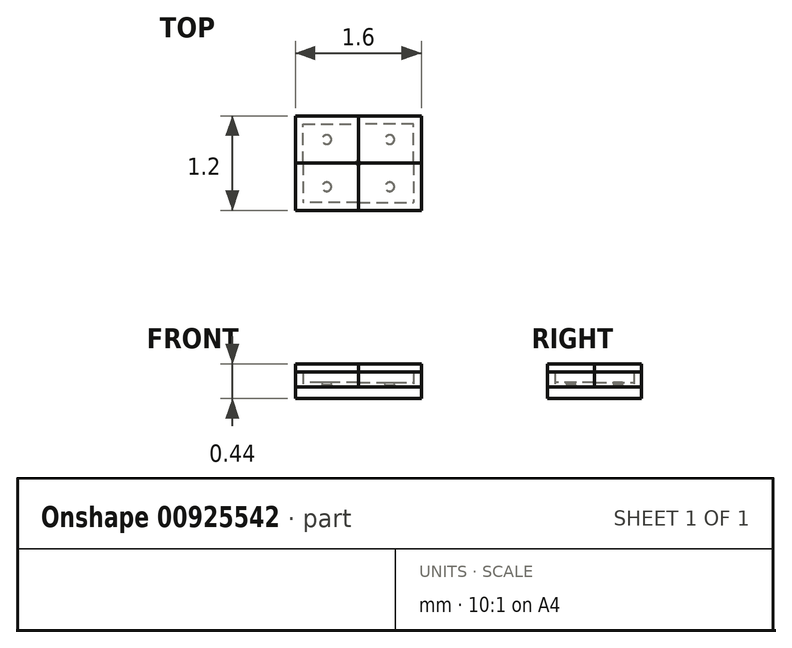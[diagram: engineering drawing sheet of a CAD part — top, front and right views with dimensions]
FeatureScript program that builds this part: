
annotation { "Feature Type Name" : "Feature", "Feature Type Description" : "" }
export const myFeature = defineFeature(function(context is Context, id is Id, definition is map)
    precondition{}
    {
        {
            var Q0;
            Q0=qCreatedBy(makeId("Top.planeOp"),FACE);
            var sketch = newSketch(context, id + "F0", { "sketchPlane" : qUnion([Q0])});
            skLineSegment(sketch, "E0.bottom", {"start": v(0, 0) * mm, "end": v(-0.8, 0) * mm});
            skLineSegment(sketch, "E0.top", {"start": v(0, 0.6) * mm, "end": v(-0.8, 0.6) * mm});
            skLineSegment(sketch, "E0.left", {"start": v(0, 0) * mm, "end": v(0, 0.6) * mm});
            skLineSegment(sketch, "E0.right", {"start": v(-0.8, 0) * mm, "end": v(-0.8, 0.6) * mm});
            skLineSegment(sketch, "E1", {"start": v(-0.8, 0.3) * mm, "end": v(0, 0.3) * mm, "construction": true});
            skSolve(sketch);
        }
        {
            var Q0;
            Q0 = qSketchRegion(id + "F0", true);
            extrude(context, id + "F1", {"entities" : qUnion([Q0]), "depth" : 0.15 * mm, "offsetDistance" : 25.4 * mm});
        }
        {
            var Q0;
            Q0=makeQuery(id+"F1.opExtrude","SWEPT_FACE",FACE,{"disambiguationData":[OSD([sQuery(id+"F0.wireOp",EDGE,"E0.left")])]});
            cPlane(context, id + "F2", {"entities" : qUnion([Q0]), "cplaneType" : CPlaneType.OFFSET, "offset" : 0.4 * mm, "oppositeDirection" : true, "width" : 152.4 * mm, "height" : 152.4 * mm});
        }
        {
            var Q0;
            {var subQ0=makeQuery(id+"F1.opExtrude","CAP_FACE",FACE,{"disambiguationData":[OSD([sQuery(id+"F0.wireOp",EDGE,"E0.bottom"),sQuery(id+"F0.wireOp",EDGE,"E0.top"),sQuery(id+"F0.wireOp",EDGE,"E0.left"),sQuery(id+"F0.wireOp",EDGE,"E0.right")])],"isStart":false});var subQ1=makeQuery(id+"F15.opPattern","COPY",FACE,{"derivedFrom":subQ0,"instanceName":"1"});Q0=makeQuery(id+"F17.opBoolean","MERGE",FACE,{"derivedFrom":[subQ0,subQ1,makeQuery(id+"F16.opPattern","COPY",FACE,{"derivedFrom":subQ0,"instanceName":"1"}),makeQuery(id+"F16.opPattern","COPY",FACE,{"derivedFrom":subQ1,"instanceName":"1"})]});}
            var sketch = newSketch(context, id + "F3", { "sketchPlane" : qUnion([Q0])});
            skCircle(sketch, "E2", {"center": v(-0.4, 0.3) * mm, "radius": 0.06 * mm});
            skLineSegment(sketch, "E3", {"start": v(-0.8, 0.3) * mm, "end": v(0, 0.3) * mm, "construction": true});
            skSolve(sketch);
        }
        {
            var Q0;
            Q0 = qSketchRegion(id + "F3", true);
            extrude(context, id + "F4", {"entities" : qUnion([Q0]), "depth" : 0.03 * mm, "offsetDistance" : 25.4 * mm});
        }
        {
            var Q0;
            Q0=qCreatedBy(id+"F2.planeOp",FACE);
            var sketch = newSketch(context, id + "F5", { "sketchPlane" : qUnion([Q0])});
            skLineSegment(sketch, "E4", {"start": v(0.24, 0.18) * mm, "end": v(0.3, 0.18) * mm});
            skArc(sketch, "E5", {"start": v(0.24, 0.18) * mm, "mid": v(0.24, 0.2) * mm, "end": v(0.24, 0.2) * mm});
            skLineSegment(sketch, "E6", {"start": v(0.3, 0.2) * mm, "end": v(0.3, 0.18) * mm});
            skLineSegment(sketch, "E7", {"start": v(0.24, 0.2) * mm, "end": v(0.3, 0.2) * mm});
            skLineSegment(sketch, "E8", {"start": v(0.3, 0.2) * mm, "end": v(0.3, 0.2) * mm});
            skPoint(sketch, "E9.orphan", {"position": v(0.36, 0.18) * mm});
            skSolve(sketch);
        }
        {
            var Q0;
            Q0=makeQuery(id+"F5.imprint","IMPRINT",FACE,{"disambiguationData":[TD([[makeQuery(id+"F5.imprint","IMPRINT",EDGE,{"derivedFrom":sQuery(id+"F5.wireOp",EDGE,"E4")}),1.0]])]});
            var Q1;
            Q1=sQuery(id+"F5.wireOp",EDGE,"E8");
            revolve(context, id + "F6", {"surfaceOperationType" : NewSurfaceOperationType.NEW, "entities" : qUnion([Q0]), "axis" : qUnion([Q1]), "revolveType" : RevolveType.FULL});
        }
        {
            var Q0;
            Q0=makeQuery(id+"F6.opRevolve","SWEPT_FACE",FACE,{"disambiguationData":[OSD([sQuery(id+"F5.wireOp",EDGE,"E7")])]});
            var sketch = newSketch(context, id + "F7", { "sketchPlane" : qUnion([Q0])});
            skLineSegment(sketch, "E10.bottom", {"start": v(0, 0) * mm, "end": v(-0.7, 0) * mm});
            skLineSegment(sketch, "E10.top", {"start": v(0, 0.5) * mm, "end": v(-0.7, 0.5) * mm});
            skLineSegment(sketch, "E10.left", {"start": v(0, 0) * mm, "end": v(0, 0.5) * mm});
            skLineSegment(sketch, "E10.right", {"start": v(-0.7, 0) * mm, "end": v(-0.7, 0.5) * mm});
            skLineSegment(sketch, "E11.top", {"start": v(0, 0) * mm, "end": v(-0.03, 0) * mm});
            skLineSegment(sketch, "E11.left", {"start": v(0, 0.03) * mm, "end": v(0, 0) * mm});
            skSolve(sketch);
        }
        {
            var Q0;
            Q0 = qSketchRegion(id + "F7", true);
            extrude(context, id + "F8", {"entities" : qUnion([Q0]), "depth" : 0.13 * mm, "offsetDistance" : 25.4 * mm});
        }
        {
            var Q0;
            Q0=makeQuery(id+"F8.opExtrude","CAP_FACE",FACE,{"disambiguationData":[OSD([sQuery(id+"F7.wireOp",EDGE,"E10.bottom"),sQuery(id+"F7.wireOp",EDGE,"E10.top"),sQuery(id+"F7.wireOp",EDGE,"E10.left"),sQuery(id+"F7.wireOp",EDGE,"E10.right")])],"isStart":false});
            var sketch = newSketch(context, id + "F9", { "sketchPlane" : qUnion([Q0])});
            skLineSegment(sketch, "E12.bottom", {"start": v(-0.7, 0) * mm, "end": v(-0.8, 0) * mm});
            skLineSegment(sketch, "E12.top", {"start": v(-0.7, 0.6) * mm, "end": v(-0.8, 0.6) * mm});
            skLineSegment(sketch, "E12.left", {"start": v(-0.7, 0) * mm, "end": v(-0.7, 0.6) * mm});
            skLineSegment(sketch, "E12.right", {"start": v(-0.8, 0) * mm, "end": v(-0.8, 0.6) * mm});
            skLineSegment(sketch, "E13.bottom", {"start": v(-0.7, 0.6) * mm, "end": v(0, 0.6) * mm});
            skLineSegment(sketch, "E13.top", {"start": v(-0.7, 0.5) * mm, "end": v(0, 0.5) * mm});
            skLineSegment(sketch, "E13.left", {"start": v(-0.7, 0.6) * mm, "end": v(-0.7, 0.5) * mm});
            skLineSegment(sketch, "E13.right", {"start": v(0, 0.6) * mm, "end": v(0, 0.5) * mm});
            skLineSegment(sketch, "E14.top", {"start": v(-0.7, 0) * mm, "end": v(0, 0) * mm});
            skLineSegment(sketch, "E14.left", {"start": v(-0.7, 0.5) * mm, "end": v(-0.7, 0) * mm});
            skLineSegment(sketch, "E14.right", {"start": v(0, 0.5) * mm, "end": v(0, 0) * mm});
            skSolve(sketch);
        }
        {
            var Q0;
            Q0 = qSketchRegion(id + "F9", true);
            extrude(context, id + "F10", {"entities" : qUnion([Q0]), "depth" : 0.1 * mm, "offsetDistance" : 25.4 * mm});
        }
        {
            var Q0;
            Q0=makeQuery(id+"F7.imprint","IMPRINT",FACE,{"disambiguationData":[TD([[makeQuery(id+"F7.imprint","IMPRINT",EDGE,{"derivedFrom":sQuery(id+"F7.wireOp",EDGE,"E10.bottom")}),-1.0]])]});
            var sketch = newSketch(context, id + "F11", { "sketchPlane" : qUnion([Q0])});
            skLineSegment(sketch, "E15.bottom", {"start": v(0, 0) * mm, "end": v(-0.03, 0) * mm});
            skLineSegment(sketch, "E15.top", {"start": v(0, 0.03) * mm, "end": v(-0.03, 0.03) * mm});
            skLineSegment(sketch, "E15.left", {"start": v(0, 0) * mm, "end": v(0, 0.03) * mm});
            skLineSegment(sketch, "E15.right", {"start": v(-0.03, 0) * mm, "end": v(-0.03, 0.03) * mm});
            skSolve(sketch);
        }
        {
            var Q0;
            Q0=makeQuery(id+"F1.opExtrude","CAP_FACE",FACE,{"disambiguationData":[OSD([sQuery(id+"F0.wireOp",EDGE,"E0.bottom"),sQuery(id+"F0.wireOp",EDGE,"E0.top"),sQuery(id+"F0.wireOp",EDGE,"E0.left"),sQuery(id+"F0.wireOp",EDGE,"E0.right")])],"isStart":false});
            var sketch = newSketch(context, id + "F12", { "sketchPlane" : qUnion([Q0])});
            skLineSegment(sketch, "E16", {"start": v(0, 0.6) * mm, "end": v(-0.8, 0.6) * mm});
            skLineSegment(sketch, "E17", {"start": v(-0.8, 0.6) * mm, "end": v(-0.8, 0) * mm});
            skLineSegment(sketch, "E18", {"start": v(-0.8, 0) * mm, "end": v(-0.7, 0) * mm});
            skLineSegment(sketch, "E19", {"start": v(-0.7, 0) * mm, "end": v(-0.7, 0.5) * mm});
            skLineSegment(sketch, "E20", {"start": v(-0.7, 0.5) * mm, "end": v(0, 0.5) * mm});
            skLineSegment(sketch, "E21", {"start": v(0, 0.5) * mm, "end": v(0, 0.6) * mm});
            skSolve(sketch);
        }
        {
            var Q0;
            Q0 = qSketchRegion(id + "F11", true);
            extrude(context, id + "F13", {"entities" : qUnion([Q0]), "depth" : 0 * mm, "offsetDistance" : 25.4 * mm});
        }
        {
            var Q0;
            Q0 = qSketchRegion(id + "F12", true);
            extrude(context, id + "F14", {"entities" : qUnion([Q0]), "depth" : 0.19 * mm, "offsetDistance" : 25.4 * mm});
        }
        {
            var Q0;
            Q0=makeQuery(id+"F8.opExtrude","SWEPT_BODY",BODY,{"disambiguationData":[OSD([sQuery(id+"F7.wireOp",EDGE,"E10.bottom"),sQuery(id+"F7.wireOp",EDGE,"E10.top"),sQuery(id+"F7.wireOp",EDGE,"E10.left"),sQuery(id+"F7.wireOp",EDGE,"E10.right"),sQuery(id+"F7.wireOp",EDGE,"E11.top"),sQuery(id+"F7.wireOp",EDGE,"E11.left")])]});
            var Q1;
            Q1=makeQuery(id+"F10.opExtrude","SWEPT_BODY",BODY,{"disambiguationData":[OSD([sQuery(id+"F9.wireOp",EDGE,"E12.bottom"),sQuery(id+"F9.wireOp",EDGE,"E12.top"),sQuery(id+"F9.wireOp",EDGE,"E12.right"),sQuery(id+"F9.wireOp",EDGE,"E13.bottom"),sQuery(id+"F9.wireOp",EDGE,"E13.right"),sQuery(id+"F9.wireOp",EDGE,"E14.top"),sQuery(id+"F9.wireOp",EDGE,"E14.right")])]});
            var Q2;
            Q2=makeQuery(id+"F6.opRevolve","SWEPT_BODY",BODY,{"disambiguationData":[OSD([sQuery(id+"F5.wireOp",EDGE,"E4"),sQuery(id+"F5.wireOp",EDGE,"E5"),sQuery(id+"F5.wireOp",EDGE,"E6"),sQuery(id+"F5.wireOp",EDGE,"E7"),sQuery(id+"F5.wireOp",EDGE,"E8")])]});
            var Q3;
            Q3=makeQuery(id+"F13.opExtrude","SWEPT_BODY",BODY,{"disambiguationData":[OSD([sQuery(id+"F11.wireOp",EDGE,"E15.bottom"),sQuery(id+"F11.wireOp",EDGE,"E15.top"),sQuery(id+"F11.wireOp",EDGE,"E15.left"),sQuery(id+"F11.wireOp",EDGE,"E15.right")])]});
            var Q4;
            Q4=makeQuery(id+"F1.opExtrude","SWEPT_BODY",BODY,{"disambiguationData":[OSD([sQuery(id+"F0.wireOp",EDGE,"E0.bottom"),sQuery(id+"F0.wireOp",EDGE,"E0.top"),sQuery(id+"F0.wireOp",EDGE,"E0.left"),sQuery(id+"F0.wireOp",EDGE,"E0.right")])]});
            var Q5;
            Q5=makeQuery(id+"F4.opExtrude","SWEPT_BODY",BODY,{"disambiguationData":[OSD([sQuery(id+"F3.wireOp",EDGE,"E2")])]});
            var Q6;
            Q6=makeQuery(id+"F14.opExtrude","SWEPT_BODY",BODY,{"disambiguationData":[OSD([sQuery(id+"F12.wireOp",EDGE,"E16"),sQuery(id+"F12.wireOp",EDGE,"E17"),sQuery(id+"F12.wireOp",EDGE,"E18"),sQuery(id+"F12.wireOp",EDGE,"E19"),sQuery(id+"F12.wireOp",EDGE,"E20"),sQuery(id+"F12.wireOp",EDGE,"E21")])]});
            var Q7;
            Q7=makeQuery(id+"F8.opExtrude","SWEPT_FACE",FACE,{"disambiguationData":[OSD([sQuery(id+"F7.wireOp",EDGE,"E10.left")])]});
            mirror(context, id + "F15", {"entities" : qUnion([Q0, Q1, Q2, Q3, Q4, Q5, Q6]), "mirrorPlane" : qUnion([Q7])});
        }
        {
            var Q0;
            Q0=makeQuery(id+"F15.opPattern","COPY",BODY,{"derivedFrom":makeQuery(id+"F10.opExtrude","SWEPT_BODY",BODY,{"disambiguationData":[OSD([sQuery(id+"F9.wireOp",EDGE,"E12.bottom"),sQuery(id+"F9.wireOp",EDGE,"E12.top"),sQuery(id+"F9.wireOp",EDGE,"E12.right"),sQuery(id+"F9.wireOp",EDGE,"E13.bottom"),sQuery(id+"F9.wireOp",EDGE,"E13.right"),sQuery(id+"F9.wireOp",EDGE,"E14.top"),sQuery(id+"F9.wireOp",EDGE,"E14.right")])]}),"instanceName":"1"});
            var Q1;
            Q1=makeQuery(id+"F15.opPattern","COPY",BODY,{"derivedFrom":makeQuery(id+"F13.opExtrude","SWEPT_BODY",BODY,{"disambiguationData":[OSD([sQuery(id+"F11.wireOp",EDGE,"E15.bottom"),sQuery(id+"F11.wireOp",EDGE,"E15.top"),sQuery(id+"F11.wireOp",EDGE,"E15.left"),sQuery(id+"F11.wireOp",EDGE,"E15.right")])]}),"instanceName":"1"});
            var Q2;
            Q2=makeQuery(id+"F15.opPattern","COPY",BODY,{"derivedFrom":makeQuery(id+"F8.opExtrude","SWEPT_BODY",BODY,{"disambiguationData":[OSD([sQuery(id+"F7.wireOp",EDGE,"E10.bottom"),sQuery(id+"F7.wireOp",EDGE,"E10.top"),sQuery(id+"F7.wireOp",EDGE,"E10.left"),sQuery(id+"F7.wireOp",EDGE,"E10.right"),sQuery(id+"F7.wireOp",EDGE,"E11.top"),sQuery(id+"F7.wireOp",EDGE,"E11.left")])]}),"instanceName":"1"});
            var Q3;
            Q3=makeQuery(id+"F10.opExtrude","SWEPT_BODY",BODY,{"disambiguationData":[OSD([sQuery(id+"F9.wireOp",EDGE,"E12.bottom"),sQuery(id+"F9.wireOp",EDGE,"E12.top"),sQuery(id+"F9.wireOp",EDGE,"E12.right"),sQuery(id+"F9.wireOp",EDGE,"E13.bottom"),sQuery(id+"F9.wireOp",EDGE,"E13.right"),sQuery(id+"F9.wireOp",EDGE,"E14.top"),sQuery(id+"F9.wireOp",EDGE,"E14.right")])]});
            var Q4;
            Q4=makeQuery(id+"F13.opExtrude","SWEPT_BODY",BODY,{"disambiguationData":[OSD([sQuery(id+"F11.wireOp",EDGE,"E15.bottom"),sQuery(id+"F11.wireOp",EDGE,"E15.top"),sQuery(id+"F11.wireOp",EDGE,"E15.left"),sQuery(id+"F11.wireOp",EDGE,"E15.right")])]});
            var Q5;
            Q5=makeQuery(id+"F15.opPattern","COPY",BODY,{"derivedFrom":makeQuery(id+"F1.opExtrude","SWEPT_BODY",BODY,{"disambiguationData":[OSD([sQuery(id+"F0.wireOp",EDGE,"E0.bottom"),sQuery(id+"F0.wireOp",EDGE,"E0.top"),sQuery(id+"F0.wireOp",EDGE,"E0.left"),sQuery(id+"F0.wireOp",EDGE,"E0.right")])]}),"instanceName":"1"});
            var Q6;
            Q6=makeQuery(id+"F8.opExtrude","SWEPT_BODY",BODY,{"disambiguationData":[OSD([sQuery(id+"F7.wireOp",EDGE,"E10.bottom"),sQuery(id+"F7.wireOp",EDGE,"E10.top"),sQuery(id+"F7.wireOp",EDGE,"E10.left"),sQuery(id+"F7.wireOp",EDGE,"E10.right"),sQuery(id+"F7.wireOp",EDGE,"E11.top"),sQuery(id+"F7.wireOp",EDGE,"E11.left")])]});
            var Q7;
            Q7=makeQuery(id+"F6.opRevolve","SWEPT_BODY",BODY,{"disambiguationData":[OSD([sQuery(id+"F5.wireOp",EDGE,"E4"),sQuery(id+"F5.wireOp",EDGE,"E5"),sQuery(id+"F5.wireOp",EDGE,"E6"),sQuery(id+"F5.wireOp",EDGE,"E7"),sQuery(id+"F5.wireOp",EDGE,"E8")])]});
            var Q8;
            Q8=makeQuery(id+"F1.opExtrude","SWEPT_BODY",BODY,{"disambiguationData":[OSD([sQuery(id+"F0.wireOp",EDGE,"E0.bottom"),sQuery(id+"F0.wireOp",EDGE,"E0.top"),sQuery(id+"F0.wireOp",EDGE,"E0.left"),sQuery(id+"F0.wireOp",EDGE,"E0.right")])]});
            var Q9;
            Q9=makeQuery(id+"F15.opPattern","COPY",BODY,{"derivedFrom":makeQuery(id+"F6.opRevolve","SWEPT_BODY",BODY,{"disambiguationData":[OSD([sQuery(id+"F5.wireOp",EDGE,"E4"),sQuery(id+"F5.wireOp",EDGE,"E5"),sQuery(id+"F5.wireOp",EDGE,"E6"),sQuery(id+"F5.wireOp",EDGE,"E7"),sQuery(id+"F5.wireOp",EDGE,"E8")])]}),"instanceName":"1"});
            var Q10;
            Q10=makeQuery(id+"F4.opExtrude","SWEPT_BODY",BODY,{"disambiguationData":[OSD([sQuery(id+"F3.wireOp",EDGE,"E2")])]});
            var Q11;
            Q11=makeQuery(id+"F15.opPattern","COPY",BODY,{"derivedFrom":makeQuery(id+"F4.opExtrude","SWEPT_BODY",BODY,{"disambiguationData":[OSD([sQuery(id+"F3.wireOp",EDGE,"E2")])]}),"instanceName":"1"});
            var Q12;
            Q12=makeQuery(id+"F14.opExtrude","SWEPT_BODY",BODY,{"disambiguationData":[OSD([sQuery(id+"F12.wireOp",EDGE,"E16"),sQuery(id+"F12.wireOp",EDGE,"E17"),sQuery(id+"F12.wireOp",EDGE,"E18"),sQuery(id+"F12.wireOp",EDGE,"E19"),sQuery(id+"F12.wireOp",EDGE,"E20"),sQuery(id+"F12.wireOp",EDGE,"E21")])]});
            var Q13;
            Q13=makeQuery(id+"F15.opPattern","COPY",BODY,{"derivedFrom":makeQuery(id+"F14.opExtrude","SWEPT_BODY",BODY,{"disambiguationData":[OSD([sQuery(id+"F12.wireOp",EDGE,"E16"),sQuery(id+"F12.wireOp",EDGE,"E17"),sQuery(id+"F12.wireOp",EDGE,"E18"),sQuery(id+"F12.wireOp",EDGE,"E19"),sQuery(id+"F12.wireOp",EDGE,"E20"),sQuery(id+"F12.wireOp",EDGE,"E21")])]}),"instanceName":"1"});
            var Q14;
            Q14=makeQuery(id+"F10.opExtrude","SWEPT_FACE",FACE,{"disambiguationData":[OSD([sQuery(id+"F9.wireOp",EDGE,"E12.bottom")])]});
            mirror(context, id + "F16", {"entities" : qUnion([Q0, Q1, Q2, Q3, Q4, Q5, Q6, Q7, Q8, Q9, Q10, Q11, Q12, Q13]), "mirrorPlane" : qUnion([Q14])});
        }
        {
            var Q0;
            Q0=makeQuery(id+"F15.opPattern","COPY",BODY,{"derivedFrom":makeQuery(id+"F1.opExtrude","SWEPT_BODY",BODY,{"disambiguationData":[OSD([sQuery(id+"F0.wireOp",EDGE,"E0.bottom"),sQuery(id+"F0.wireOp",EDGE,"E0.top"),sQuery(id+"F0.wireOp",EDGE,"E0.left"),sQuery(id+"F0.wireOp",EDGE,"E0.right")])]}),"instanceName":"1"});
            var Q1;
            Q1=makeQuery(id+"F1.opExtrude","SWEPT_BODY",BODY,{"disambiguationData":[OSD([sQuery(id+"F0.wireOp",EDGE,"E0.bottom"),sQuery(id+"F0.wireOp",EDGE,"E0.top"),sQuery(id+"F0.wireOp",EDGE,"E0.left"),sQuery(id+"F0.wireOp",EDGE,"E0.right")])]});
            var Q2;
            Q2=makeQuery(id+"F16.opPattern","COPY",BODY,{"derivedFrom":makeQuery(id+"F1.opExtrude","SWEPT_BODY",BODY,{"disambiguationData":[OSD([sQuery(id+"F0.wireOp",EDGE,"E0.bottom"),sQuery(id+"F0.wireOp",EDGE,"E0.top"),sQuery(id+"F0.wireOp",EDGE,"E0.left"),sQuery(id+"F0.wireOp",EDGE,"E0.right")])]}),"instanceName":"1"});
            var Q3;
            Q3=makeQuery(id+"F16.opPattern","COPY",BODY,{"derivedFrom":makeQuery(id+"F15.opPattern","COPY",BODY,{"derivedFrom":makeQuery(id+"F1.opExtrude","SWEPT_BODY",BODY,{"disambiguationData":[OSD([sQuery(id+"F0.wireOp",EDGE,"E0.bottom"),sQuery(id+"F0.wireOp",EDGE,"E0.top"),sQuery(id+"F0.wireOp",EDGE,"E0.left"),sQuery(id+"F0.wireOp",EDGE,"E0.right")])]}),"instanceName":"1"}),"instanceName":"1"});
            booleanBodies(context, id + "F17", {"operationType" : BooleanOperationType.UNION, "tools" : qUnion([Q0, Q1, Q2, Q3])});
        }
    });
